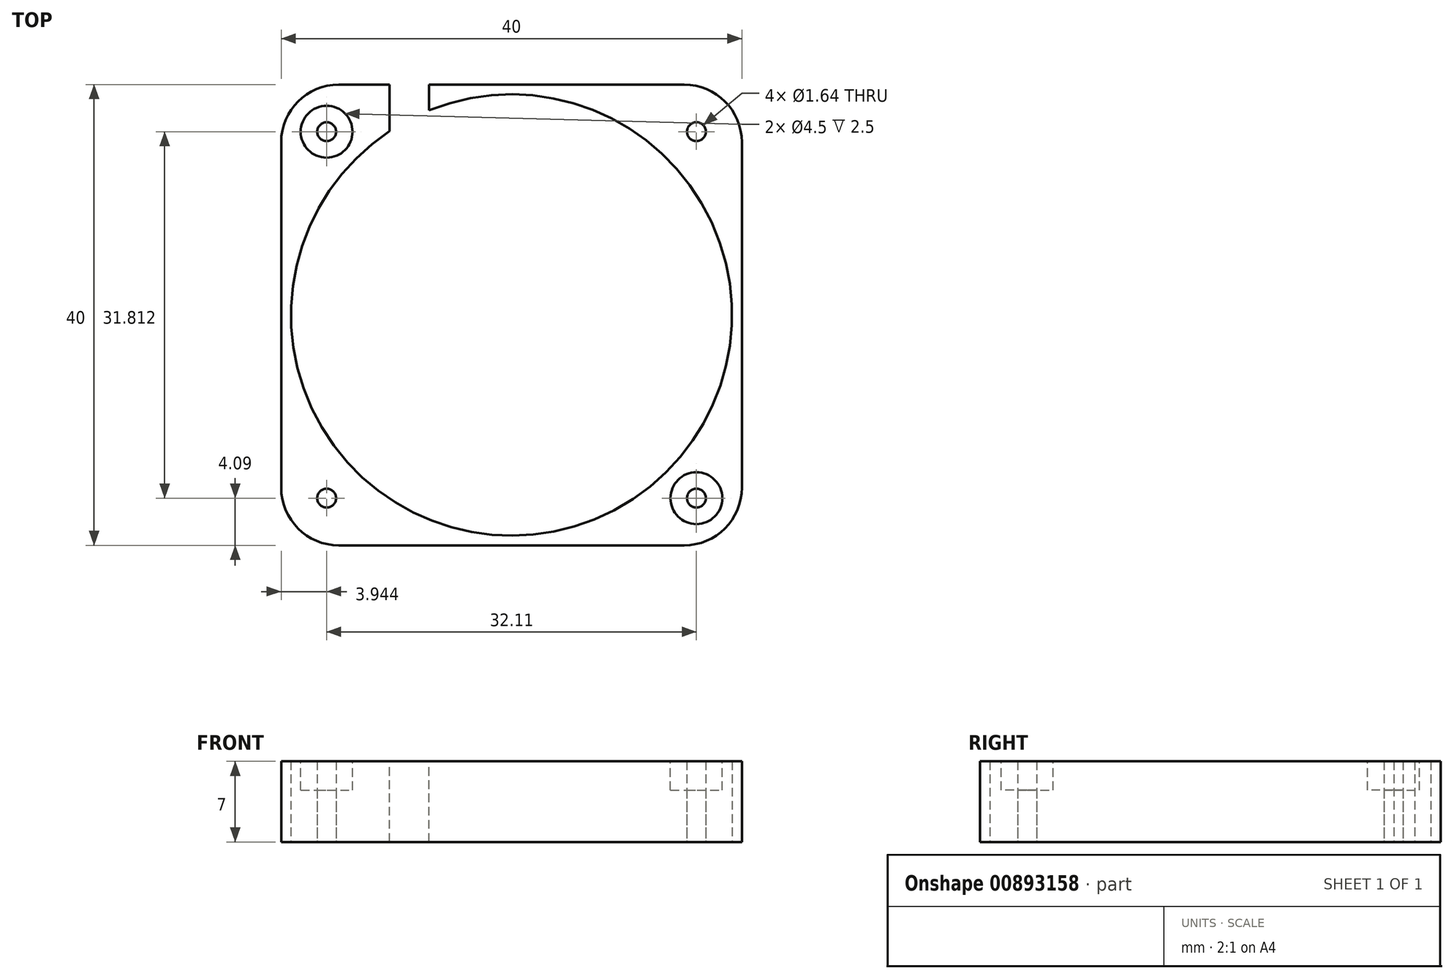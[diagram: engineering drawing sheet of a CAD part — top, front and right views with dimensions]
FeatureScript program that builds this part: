
annotation { "Feature Type Name" : "Feature", "Feature Type Description" : "" }
export const myFeature = defineFeature(function(context is Context, id is Id, definition is map)
    precondition{}
    {
        {
            var Q0;
            Q0=qCreatedBy(makeId("Top.planeOp"),FACE);
            var sketch = newSketch(context, id + "F0", { "sketchPlane" : qUnion([Q0])});
            skCircle(sketch, "E0", {"center": v(-57.98, 66.95) * mm, "radius": 2 * mm});
            skCircle(sketch, "E1", {"center": v(-25.87, 66.95) * mm, "radius": 2 * mm});
            skCircle(sketch, "E2", {"center": v(-25.87, 35.14) * mm, "radius": 2 * mm});
            skCircle(sketch, "E3", {"center": v(-57.98, 35.14) * mm, "radius": 2 * mm});
            skLineSegment(sketch, "E4.bottom", {"start": v(-21.92, 31.05) * mm, "end": v(-61.92, 31.05) * mm});
            skLineSegment(sketch, "E4.top", {"start": v(-21.92, 71.05) * mm, "end": v(-61.92, 71.05) * mm});
            skLineSegment(sketch, "E4.left", {"start": v(-21.92, 31.05) * mm, "end": v(-21.92, 71.05) * mm});
            skLineSegment(sketch, "E4.right", {"start": v(-61.92, 31.05) * mm, "end": v(-61.92, 71.05) * mm});
            skPoint(sketch, "E4.middle", {"position": v(-41.92, 51.05) * mm});
            skPoint(sketch, "E5", {"position": v(-61.92, 63.55) * mm});
            skPoint(sketch, "E6", {"position": v(-21.92, 63.55) * mm});
            skPoint(sketch, "E7", {"position": v(-61.92, 38.55) * mm});
            skPoint(sketch, "E8", {"position": v(-21.92, 38.55) * mm});
            skPoint(sketch, "E9", {"position": v(-54.42, 71.05) * mm});
            skPoint(sketch, "E10", {"position": v(-29.42, 71.05) * mm});
            skPoint(sketch, "E11", {"position": v(-29.42, 31.05) * mm});
            skPoint(sketch, "E12", {"position": v(-54.42, 31.05) * mm});
            skLineSegment(sketch, "E13", {"start": v(-61.92, 63.55) * mm, "end": v(-54.42, 63.55) * mm});
            skLineSegment(sketch, "E14", {"start": v(-54.42, 63.55) * mm, "end": v(-54.42, 71.05) * mm});
            skLineSegment(sketch, "E15", {"start": v(-29.42, 71.05) * mm, "end": v(-29.42, 63.55) * mm});
            skLineSegment(sketch, "E16", {"start": v(-29.42, 63.55) * mm, "end": v(-21.92, 63.55) * mm});
            skLineSegment(sketch, "E17", {"start": v(-61.92, 38.55) * mm, "end": v(-54.42, 38.55) * mm});
            skLineSegment(sketch, "E18", {"start": v(-54.42, 38.55) * mm, "end": v(-54.42, 31.05) * mm});
            skLineSegment(sketch, "E19", {"start": v(-21.92, 38.55) * mm, "end": v(-29.42, 38.55) * mm});
            skLineSegment(sketch, "E20", {"start": v(-29.42, 38.55) * mm, "end": v(-29.42, 31.05) * mm});
            skPoint(sketch, "E21", {"position": v(-59.92, 63.55) * mm});
            skPoint(sketch, "E22", {"position": v(-59.92, 38.55) * mm});
            skPoint(sketch, "E23", {"position": v(-54.42, 33.05) * mm});
            skPoint(sketch, "E24", {"position": v(-29.42, 33.05) * mm});
            skPoint(sketch, "E25", {"position": v(-23.92, 38.55) * mm});
            skPoint(sketch, "E26", {"position": v(-23.92, 63.55) * mm});
            skPoint(sketch, "E27", {"position": v(-29.42, 69.05) * mm});
            skPoint(sketch, "E28", {"position": v(-54.42, 69.05) * mm});
            skLineSegment(sketch, "E29", {"start": v(-59.92, 63.55) * mm, "end": v(-59.92, 38.55) * mm});
            skLineSegment(sketch, "E30", {"start": v(-54.42, 33.05) * mm, "end": v(-29.42, 33.05) * mm});
            skLineSegment(sketch, "E31", {"start": v(-23.92, 38.55) * mm, "end": v(-23.92, 63.55) * mm});
            skLineSegment(sketch, "E32", {"start": v(-29.42, 69.05) * mm, "end": v(-54.42, 69.05) * mm});
            skCircle(sketch, "E33", {"center": v(-41.92, 51.05) * mm, "radius": 19.15 * mm});
            skSolve(sketch);
        }
        {
            var Q0;
            Q0=makeQuery(id+"F0.imprint","IMPRINT",FACE,{"disambiguationData":[TD([[makeQuery(id+"F0.imprint","IMPRINT",EDGE,{"derivedFrom":sQuery(id+"F0.wireOp",EDGE,"E1")}),-1.0]])]});
            var Q1;
            {var subQ0=sQuery(id+"F0.wireOp",EDGE,"E32");var subQ1=sQuery(id+"F0.wireOp",EDGE,"E15");var subQ2=makeQuery(id+"F0.imprint","INTERSECT",VERTEX,{"derivedFrom":[subQ1,subQ0]});Q1=makeQuery(id+"F0.imprint","IMPRINT",FACE,{"disambiguationData":[TD([[makeQuery(id+"F0.imprint","IMPRINT",EDGE,{"disambiguationData":[TD([[subQ2,-1.0]])],"derivedFrom":subQ1}),-1.0]])]});}
            var Q2;
            {var subQ5=sQuery(id+"F0.wireOp",EDGE,"E4.top");var subQ8=sQuery(id+"F0.wireOp",EDGE,"E14");var subQ9=makeQuery(id+"F0.imprint","INTERSECT",VERTEX,{"derivedFrom":[subQ5,subQ8]});Q2=makeQuery(id+"F0.imprint","IMPRINT",FACE,{"disambiguationData":[TD([[makeQuery(id+"F0.imprint","IMPRINT",EDGE,{"disambiguationData":[TD([[subQ9,1.0]])],"derivedFrom":subQ5}),1.0]])]});}
            var Q3;
            {var subQ0=sQuery(id+"F0.wireOp",EDGE,"E32");var subQ1=sQuery(id+"F0.wireOp",EDGE,"E14");var subQ2=makeQuery(id+"F0.imprint","INTERSECT",VERTEX,{"derivedFrom":[subQ1,subQ0]});Q3=makeQuery(id+"F0.imprint","IMPRINT",FACE,{"disambiguationData":[TD([[makeQuery(id+"F0.imprint","IMPRINT",EDGE,{"disambiguationData":[TD([[subQ2,1.0]])],"derivedFrom":subQ1}),-1.0]])]});}
            var Q4;
            Q4=makeQuery(id+"F0.imprint","IMPRINT",FACE,{"disambiguationData":[TD([[makeQuery(id+"F0.imprint","IMPRINT",EDGE,{"derivedFrom":sQuery(id+"F0.wireOp",EDGE,"E0")}),-1.0]])]});
            var Q5;
            {var subQ0=sQuery(id+"F0.wireOp",EDGE,"E29");var subQ1=sQuery(id+"F0.wireOp",EDGE,"E13");var subQ2=makeQuery(id+"F0.imprint","INTERSECT",VERTEX,{"derivedFrom":[subQ1,subQ0]});Q5=makeQuery(id+"F0.imprint","IMPRINT",FACE,{"disambiguationData":[TD([[makeQuery(id+"F0.imprint","IMPRINT",EDGE,{"disambiguationData":[TD([[subQ2,-1.0]])],"derivedFrom":subQ1}),-1.0]])]});}
            var Q6;
            {var subQ1=sQuery(id+"F0.wireOp",EDGE,"E13");var subQ6=sQuery(id+"F0.wireOp",EDGE,"E4.right");var subQ9=makeQuery(id+"F0.imprint","INTERSECT",VERTEX,{"derivedFrom":[subQ6,subQ1]});Q6=makeQuery(id+"F0.imprint","IMPRINT",FACE,{"disambiguationData":[TD([[makeQuery(id+"F0.imprint","IMPRINT",EDGE,{"disambiguationData":[TD([[subQ9,1.0]])],"derivedFrom":subQ6}),-1.0]])]});}
            var Q7;
            {var subQ0=sQuery(id+"F0.wireOp",EDGE,"E29");var subQ1=sQuery(id+"F0.wireOp",EDGE,"E17");var subQ2=makeQuery(id+"F0.imprint","INTERSECT",VERTEX,{"derivedFrom":[subQ1,subQ0]});Q7=makeQuery(id+"F0.imprint","IMPRINT",FACE,{"disambiguationData":[TD([[makeQuery(id+"F0.imprint","IMPRINT",EDGE,{"disambiguationData":[TD([[subQ2,-1.0]])],"derivedFrom":subQ1}),1.0]])]});}
            var Q8;
            Q8=makeQuery(id+"F0.imprint","IMPRINT",FACE,{"disambiguationData":[TD([[makeQuery(id+"F0.imprint","IMPRINT",EDGE,{"derivedFrom":sQuery(id+"F0.wireOp",EDGE,"E3")}),-1.0]])]});
            var Q9;
            {var subQ0=sQuery(id+"F0.wireOp",EDGE,"E30");var subQ1=sQuery(id+"F0.wireOp",EDGE,"E18");var subQ2=makeQuery(id+"F0.imprint","INTERSECT",VERTEX,{"derivedFrom":[subQ1,subQ0]});Q9=makeQuery(id+"F0.imprint","IMPRINT",FACE,{"disambiguationData":[TD([[makeQuery(id+"F0.imprint","IMPRINT",EDGE,{"disambiguationData":[TD([[subQ2,1.0]])],"derivedFrom":subQ1}),1.0]])]});}
            var Q10;
            {var subQ1=sQuery(id+"F0.wireOp",EDGE,"E4.bottom");var subQ5=sQuery(id+"F0.wireOp",EDGE,"E18");var subQ9=makeQuery(id+"F0.imprint","INTERSECT",VERTEX,{"derivedFrom":[subQ1,subQ5]});Q10=makeQuery(id+"F0.imprint","IMPRINT",FACE,{"disambiguationData":[TD([[makeQuery(id+"F0.imprint","IMPRINT",EDGE,{"disambiguationData":[TD([[subQ9,1.0]])],"derivedFrom":subQ1}),-1.0]])]});}
            var Q11;
            {var subQ0=sQuery(id+"F0.wireOp",EDGE,"E30");var subQ1=sQuery(id+"F0.wireOp",EDGE,"E20");var subQ2=makeQuery(id+"F0.imprint","INTERSECT",VERTEX,{"derivedFrom":[subQ1,subQ0]});Q11=makeQuery(id+"F0.imprint","IMPRINT",FACE,{"disambiguationData":[TD([[makeQuery(id+"F0.imprint","IMPRINT",EDGE,{"disambiguationData":[TD([[subQ2,1.0]])],"derivedFrom":subQ1}),-1.0]])]});}
            var Q12;
            Q12=makeQuery(id+"F0.imprint","IMPRINT",FACE,{"disambiguationData":[TD([[makeQuery(id+"F0.imprint","IMPRINT",EDGE,{"derivedFrom":sQuery(id+"F0.wireOp",EDGE,"E2")}),-1.0]])]});
            var Q13;
            {var subQ0=sQuery(id+"F0.wireOp",EDGE,"E31");var subQ1=sQuery(id+"F0.wireOp",EDGE,"E19");var subQ2=makeQuery(id+"F0.imprint","INTERSECT",VERTEX,{"derivedFrom":[subQ1,subQ0]});Q13=makeQuery(id+"F0.imprint","IMPRINT",FACE,{"disambiguationData":[TD([[makeQuery(id+"F0.imprint","IMPRINT",EDGE,{"disambiguationData":[TD([[subQ2,-1.0]])],"derivedFrom":subQ1}),-1.0]])]});}
            var Q14;
            {var subQ1=sQuery(id+"F0.wireOp",EDGE,"E4.left");var subQ8=sQuery(id+"F0.wireOp",EDGE,"E16");var subQ9=makeQuery(id+"F0.imprint","INTERSECT",VERTEX,{"derivedFrom":[subQ1,subQ8]});Q14=makeQuery(id+"F0.imprint","IMPRINT",FACE,{"disambiguationData":[TD([[makeQuery(id+"F0.imprint","IMPRINT",EDGE,{"disambiguationData":[TD([[subQ9,1.0]])],"derivedFrom":subQ1}),1.0]])]});}
            var Q15;
            {var subQ0=sQuery(id+"F0.wireOp",EDGE,"E31");var subQ1=sQuery(id+"F0.wireOp",EDGE,"E16");var subQ2=makeQuery(id+"F0.imprint","INTERSECT",VERTEX,{"derivedFrom":[subQ1,subQ0]});Q15=makeQuery(id+"F0.imprint","IMPRINT",FACE,{"disambiguationData":[TD([[makeQuery(id+"F0.imprint","IMPRINT",EDGE,{"disambiguationData":[TD([[subQ2,1.0]])],"derivedFrom":subQ1}),-1.0]])]});}
            extrude(context, id + "F1", {"entities" : qUnion([Q0, Q1, Q2, Q3, Q4, Q5, Q6, Q7, Q8, Q9, Q10, Q11, Q12, Q13, Q14, Q15]), "depth" : 7 * mm, "offsetDistance" : 25 * mm});
        }
        {
            var Q0;
            Q0=makeQuery(id+"F1.opExtrude","SWEPT_EDGE",EDGE,{"disambiguationData":[OSD([sQuery(id+"F0.wireOp",EDGE,"E4.bottom"),sQuery(id+"F0.wireOp",EDGE,"E4.left")])]});
            var Q1;
            Q1=makeQuery(id+"F1.opExtrude","SWEPT_EDGE",EDGE,{"disambiguationData":[OSD([sQuery(id+"F0.wireOp",EDGE,"E4.bottom"),sQuery(id+"F0.wireOp",EDGE,"E4.right")])]});
            var Q2;
            Q2=makeQuery(id+"F1.opExtrude","SWEPT_EDGE",EDGE,{"disambiguationData":[OSD([sQuery(id+"F0.wireOp",EDGE,"E4.top"),sQuery(id+"F0.wireOp",EDGE,"E4.left")])]});
            var Q3;
            Q3=makeQuery(id+"F1.opExtrude","SWEPT_EDGE",EDGE,{"disambiguationData":[OSD([sQuery(id+"F0.wireOp",EDGE,"E4.top"),sQuery(id+"F0.wireOp",EDGE,"E4.right")])]});
            fillet(context, id + "F2", {"entities" : qUnion([Q0, Q1, Q2, Q3]), "radius" : 5 * mm, "tangentPropagation" : true, "allowEdgeOverflow" : false});
        }
        {
            var Q0;
            Q0=makeQuery(id+"F1.opExtrude","CAP_FACE",FACE,{"disambiguationData":[OSD([sQuery(id+"F0.wireOp",EDGE,"E0"),sQuery(id+"F0.wireOp",EDGE,"E1"),sQuery(id+"F0.wireOp",EDGE,"E2"),sQuery(id+"F0.wireOp",EDGE,"E3"),sQuery(id+"F0.wireOp",EDGE,"E4.bottom"),sQuery(id+"F0.wireOp",EDGE,"E4.top"),sQuery(id+"F0.wireOp",EDGE,"E4.left"),sQuery(id+"F0.wireOp",EDGE,"E4.right"),sQuery(id+"F0.wireOp",EDGE,"E33")])],"isStart":false});
            var sketch = newSketch(context, id + "F3", { "sketchPlane" : qUnion([Q0])});
            skLineSegment(sketch, "E34.bottom", {"start": v(-52.5, 71.05) * mm, "end": v(-49.08, 71.05) * mm});
            skLineSegment(sketch, "E34.top", {"start": v(-52.5, 66.5) * mm, "end": v(-49.08, 66.5) * mm});
            skLineSegment(sketch, "E34.left", {"start": v(-52.5, 71.05) * mm, "end": v(-52.5, 66.5) * mm});
            skLineSegment(sketch, "E34.right", {"start": v(-49.08, 71.05) * mm, "end": v(-49.08, 66.5) * mm});
            skSolve(sketch);
        }
        {
            var Q0;
            Q0 = qSketchRegion(id + "F3", true);
            extrude(context, id + "F4", {"entities" : qUnion([Q0]), "operationType" : NewBodyOperationType.REMOVE, "oppositeDirection" : true, "depth" : 25 * mm, "offsetDistance" : 25 * mm});
        }
        {
            var Q0;
            Q0=makeQuery(id+"F1.opExtrude","CAP_FACE",FACE,{"disambiguationData":[OSD([sQuery(id+"F0.wireOp",EDGE,"E0"),sQuery(id+"F0.wireOp",EDGE,"E1"),sQuery(id+"F0.wireOp",EDGE,"E2"),sQuery(id+"F0.wireOp",EDGE,"E3"),sQuery(id+"F0.wireOp",EDGE,"E4.bottom"),sQuery(id+"F0.wireOp",EDGE,"E4.top"),sQuery(id+"F0.wireOp",EDGE,"E4.left"),sQuery(id+"F0.wireOp",EDGE,"E4.right"),sQuery(id+"F0.wireOp",EDGE,"E33")])],"isStart":false});
            var sketch = newSketch(context, id + "F5", { "sketchPlane" : qUnion([Q0])});
            skCircle(sketch, "E35", {"center": v(-57.98, 66.95) * mm, "radius": 2.25 * mm});
            skCircle(sketch, "E36", {"center": v(-25.87, 66.95) * mm, "radius": 2.25 * mm});
            skCircle(sketch, "E37", {"center": v(-25.87, 35.14) * mm, "radius": 2.25 * mm});
            skCircle(sketch, "E38", {"center": v(-57.98, 35.14) * mm, "radius": 2.25 * mm});
            skSolve(sketch);
        }
        {
            var Q0;
            Q0 = qSketchRegion(id + "F5", true);
            extrude(context, id + "F6", {"entities" : qUnion([Q0]), "operationType" : NewBodyOperationType.REMOVE, "oppositeDirection" : true, "depth" : 25 * mm, "offsetDistance" : 25 * mm});
        }
        {
            var Q0;
            Q0=makeQuery(id+"F1.opExtrude","CAP_FACE",FACE,{"disambiguationData":[OSD([sQuery(id+"F0.wireOp",EDGE,"E0"),sQuery(id+"F0.wireOp",EDGE,"E1"),sQuery(id+"F0.wireOp",EDGE,"E2"),sQuery(id+"F0.wireOp",EDGE,"E3"),sQuery(id+"F0.wireOp",EDGE,"E4.bottom"),sQuery(id+"F0.wireOp",EDGE,"E4.top"),sQuery(id+"F0.wireOp",EDGE,"E4.left"),sQuery(id+"F0.wireOp",EDGE,"E4.right"),sQuery(id+"F0.wireOp",EDGE,"E33")])],"isStart":true});
            var sketch = newSketch(context, id + "F7", { "sketchPlane" : qUnion([Q0])});
            skCircle(sketch, "E39", {"center": v(-25.87, -66.95) * mm, "radius": 0.82 * mm});
            skCircle(sketch, "E40", {"center": v(-57.98, -66.95) * mm, "radius": 0.82 * mm});
            skCircle(sketch, "E41", {"center": v(-57.98, -35.14) * mm, "radius": 0.82 * mm});
            skCircle(sketch, "E42", {"center": v(-25.87, -35.14) * mm, "radius": 0.82 * mm});
            skSolve(sketch);
        }
        {
            var Q0;
            Q0=makeQuery(id+"F7.imprint","IMPRINT",FACE,{"disambiguationData":[TD([[makeQuery(id+"F7.imprint","IMPRINT",EDGE,{"derivedFrom":sQuery(id+"F7.wireOp",EDGE,"E39")}),-1.0]])]});
            var Q1;
            Q1=makeQuery(id+"F7.imprint","IMPRINT",FACE,{"disambiguationData":[TD([[makeQuery(id+"F7.imprint","IMPRINT",EDGE,{"derivedFrom":sQuery(id+"F7.wireOp",EDGE,"E40")}),-1.0]])]});
            var Q2;
            Q2=makeQuery(id+"F7.imprint","IMPRINT",FACE,{"disambiguationData":[TD([[makeQuery(id+"F7.imprint","IMPRINT",EDGE,{"derivedFrom":sQuery(id+"F7.wireOp",EDGE,"E41")}),-1.0]])]});
            var Q3;
            Q3=makeQuery(id+"F7.imprint","IMPRINT",FACE,{"disambiguationData":[TD([[makeQuery(id+"F7.imprint","IMPRINT",EDGE,{"derivedFrom":sQuery(id+"F7.wireOp",EDGE,"E42")}),-1.0]])]});
            extrude(context, id + "F8", {"entities" : qUnion([Q0, Q1, Q2, Q3]), "operationType" : NewBodyOperationType.ADD, "oppositeDirection" : true, "depth" : 2.5 * mm, "offsetDistance" : 25 * mm});
        }
        {
            var Q0;
            Q0=makeQuery(id+"F8.opExtrude","CAP_FACE",FACE,{"disambiguationData":[OSD([sQuery(id+"F0.wireOp",EDGE,"E0"),sQuery(id+"F0.wireOp",EDGE,"E1"),sQuery(id+"F0.wireOp",EDGE,"E2"),sQuery(id+"F0.wireOp",EDGE,"E3"),sQuery(id+"F0.wireOp",EDGE,"E4.bottom"),sQuery(id+"F0.wireOp",EDGE,"E4.top"),sQuery(id+"F0.wireOp",EDGE,"E4.left"),sQuery(id+"F0.wireOp",EDGE,"E4.right"),sQuery(id+"F0.wireOp",EDGE,"E33"),sQuery(id+"F5.wireOp",EDGE,"E36"),sQuery(id+"F7.wireOp",EDGE,"E39")])],"isStart":false});
            var Q1;
            Q1=makeQuery(id+"F8.opExtrude","CAP_FACE",FACE,{"disambiguationData":[OSD([sQuery(id+"F0.wireOp",EDGE,"E0"),sQuery(id+"F0.wireOp",EDGE,"E1"),sQuery(id+"F0.wireOp",EDGE,"E2"),sQuery(id+"F0.wireOp",EDGE,"E3"),sQuery(id+"F0.wireOp",EDGE,"E4.bottom"),sQuery(id+"F0.wireOp",EDGE,"E4.top"),sQuery(id+"F0.wireOp",EDGE,"E4.left"),sQuery(id+"F0.wireOp",EDGE,"E4.right"),sQuery(id+"F0.wireOp",EDGE,"E33"),sQuery(id+"F5.wireOp",EDGE,"E38"),sQuery(id+"F7.wireOp",EDGE,"E41")])],"isStart":false});
            extrude(context, id + "F9", {"entities" : qUnion([Q0, Q1]), "operationType" : NewBodyOperationType.ADD, "depth" : 4.5 * mm, "offsetDistance" : 25 * mm});
        }
        {
            var Q0;
            Q0=makeQuery(id+"F8.opExtrude","CAP_FACE",FACE,{"disambiguationData":[OSD([sQuery(id+"F0.wireOp",EDGE,"E0"),sQuery(id+"F0.wireOp",EDGE,"E1"),sQuery(id+"F0.wireOp",EDGE,"E2"),sQuery(id+"F0.wireOp",EDGE,"E3"),sQuery(id+"F0.wireOp",EDGE,"E4.bottom"),sQuery(id+"F0.wireOp",EDGE,"E4.top"),sQuery(id+"F0.wireOp",EDGE,"E4.left"),sQuery(id+"F0.wireOp",EDGE,"E4.right"),sQuery(id+"F0.wireOp",EDGE,"E33"),sQuery(id+"F5.wireOp",EDGE,"E35"),sQuery(id+"F7.wireOp",EDGE,"E40")])],"isStart":false});
            var Q1;
            Q1=makeQuery(id+"F8.opExtrude","CAP_FACE",FACE,{"disambiguationData":[OSD([sQuery(id+"F0.wireOp",EDGE,"E0"),sQuery(id+"F0.wireOp",EDGE,"E1"),sQuery(id+"F0.wireOp",EDGE,"E2"),sQuery(id+"F0.wireOp",EDGE,"E3"),sQuery(id+"F0.wireOp",EDGE,"E4.bottom"),sQuery(id+"F0.wireOp",EDGE,"E4.top"),sQuery(id+"F0.wireOp",EDGE,"E4.left"),sQuery(id+"F0.wireOp",EDGE,"E4.right"),sQuery(id+"F0.wireOp",EDGE,"E33"),sQuery(id+"F5.wireOp",EDGE,"E37"),sQuery(id+"F7.wireOp",EDGE,"E42")])],"isStart":false});
            extrude(context, id + "F10", {"entities" : qUnion([Q0, Q1]), "operationType" : NewBodyOperationType.ADD, "depth" : 2 * mm, "offsetDistance" : 25 * mm});
        }
    });
